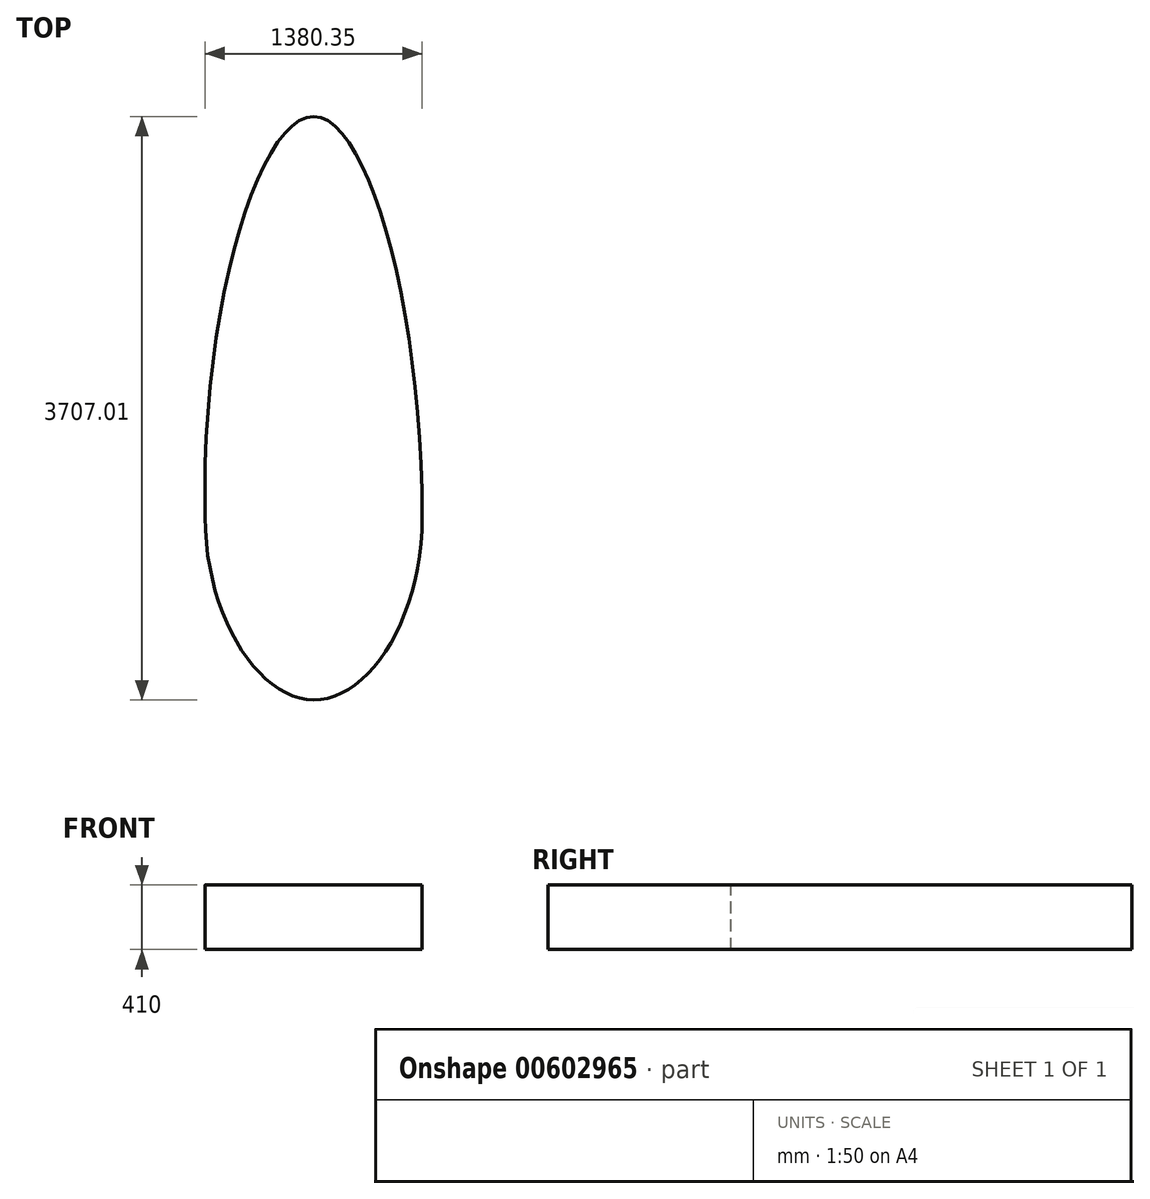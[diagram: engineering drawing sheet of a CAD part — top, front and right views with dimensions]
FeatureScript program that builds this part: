
annotation { "Feature Type Name" : "Feature", "Feature Type Description" : "" }
export const myFeature = defineFeature(function(context is Context, id is Id, definition is map)
    precondition{}
    {
        {
            var Q0;
            Q0=qCreatedBy(makeId("Front.planeOp"),FACE);
            var sketch = newSketch(context, id + "F0", { "sketchPlane" : qUnion([Q0])});
            skLineSegment(sketch, "E0", {"start": v(-690, 0) * mm, "end": v(690, 0) * mm});
            skLineSegment(sketch, "E1", {"start": v(690, 0) * mm, "end": v(690, 410) * mm});
            skLineSegment(sketch, "E2", {"start": v(-690, 0) * mm, "end": v(-690, 410) * mm});
            skLineSegment(sketch, "E3", {"start": v(0, 0) * mm, "end": v(100, 0) * mm});
            skLineSegment(sketch, "E4", {"start": v(100, 0) * mm, "end": v(100, 1000) * mm});
            skLineSegment(sketch, "E5", {"start": v(0, 0) * mm, "end": v(-100, 0) * mm});
            skLineSegment(sketch, "E6", {"start": v(-100, 0) * mm, "end": v(-100, 1000) * mm});
            skFitSpline(sketch, "E7", {"points": [v(-690, 410) * mm, v(-375, 963.38) * mm, v(-100, 1000) * mm, v(100, 1000) * mm, v(375, 963.38) * mm, v(690, 410) * mm], "startDerivative": vector(0, 1573.37) * mm, "endDerivative": vector(0, -1693.74) * mm});
            skLineSegment(sketch, "E8", {"start": v(0, 0) * mm, "end": v(375, 0) * mm});
            skLineSegment(sketch, "E9", {"start": v(0, 0) * mm, "end": v(-375, 0) * mm});
            skSolve(sketch);
        }
        {
            var Q0;
            Q0=qCreatedBy(makeId("Top.planeOp"),FACE);
            var Q1;
            Q1=sQuery(id+"F0.wireOp",VERTEX,"E7.start");
            cPlane(context, id + "F1", {"entities" : qUnion([Q0, Q1]), "cplaneType" : CPlaneType.PLANE_POINT, "offset" : 0 * mm, "width" : 150 * mm, "height" : 150 * mm});
        }
        {
            var Q0;
            Q0=qCreatedBy(id+"F1.planeOp",FACE);
            var sketch = newSketch(context, id + "F2", { "sketchPlane" : qUnion([Q0])});
            skLineSegment(sketch, "E10", {"start": v(0, 0) * mm, "end": v(0, -1162) * mm});
            skFitSpline(sketch, "E11", {"points": [v(-689.12, 0) * mm, v(0, -1162) * mm, v(689.12, 0) * mm], "startDerivative": vector(0, -3834.61) * mm, "endDerivative": vector(0, 3907.44) * mm});
            skLineSegment(sketch, "E12", {"start": v(689.12, 0) * mm, "end": v(-689.12, 0) * mm});
            skLineSegment(sketch, "E13", {"start": v(0, 0) * mm, "end": v(0, 2545) * mm});
            skFitSpline(sketch, "E14", {"points": [v(689.12, 0) * mm, v(0, 2545) * mm, v(-689.12, 0) * mm], "startDerivative": vector(0, 7757.59) * mm, "endDerivative": vector(200.53, -7804.81) * mm});
            skSolve(sketch);
        }
        {
            var Q0;
            Q0=sQuery(id+"F0.wireOp",EDGE,"E7");
            var Q1;
            Q1=sQuery(id+"F2.wireOp",EDGE,"E11");
            loft(context, id + "F3", {"bodyType" : ToolBodyType.SURFACE, "startCondition" : LoftEndDerivativeType.NORMAL_TO_PROFILE, "startMagnitude" : 1, "endCondition" : LoftEndDerivativeType.NORMAL_TO_PROFILE, "endMagnitude" : -0.55, "wireProfilesArray" : [{ "wireProfileEntities" : qUnion([Q0]) }, { "wireProfileEntities" : qUnion([Q1]) }]});
        }
        {
            var Q0;
            Q0=qSketchRegion(id+"F2",true);
            extrude(context, id + "F4", {"entities" : qUnion([Q0]), "depth" : -410 * mm, "offsetDistance" : 25 * mm});
        }
        {
            var Q0;
            Q0=sQuery(id+"F2.wireOp",EDGE,"E14");
            var Q1;
            Q1=makeQuery(id+"F3.opLoft","MID_CAP_EDGE",EDGE,{"disambiguationData":[OSD([sQuery(id+"F0.wireOp",VERTEX,"E7.start"),sQuery(id+"F0.wireOp",VERTEX,"E7.end"),sQuery(id+"F0.wireOp",EDGE,"E7")])],"capPos":0.0});
            loft(context, id + "F5", {"bodyType" : ToolBodyType.SURFACE, "endCondition" : LoftEndDerivativeType.MATCH_TANGENT, "endMagnitude" : -1, "wireProfilesArray" : [{ "wireProfileEntities" : qUnion([Q0]) }, { "wireProfileEntities" : qUnion([Q1]) }]});
        }
    });
